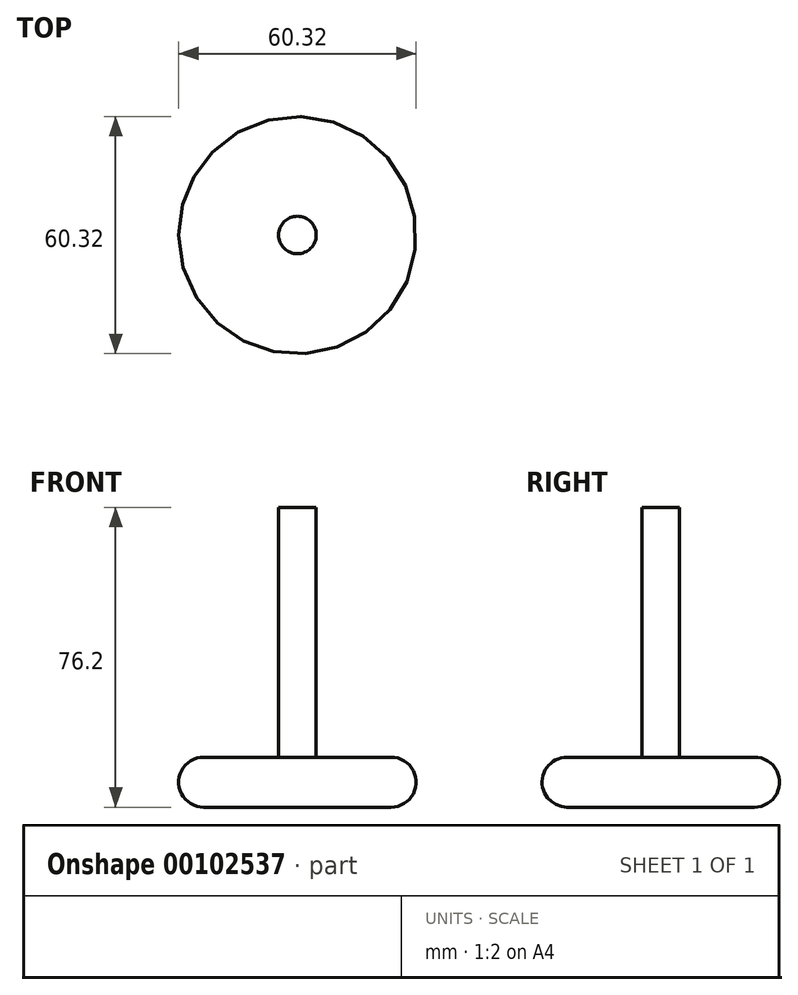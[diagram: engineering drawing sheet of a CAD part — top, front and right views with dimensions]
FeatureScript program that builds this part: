
annotation { "Feature Type Name" : "Feature", "Feature Type Description" : "" }
export const myFeature = defineFeature(function(context is Context, id is Id, definition is map)
    precondition{}
    {
        {
            var Q0;
            Q0=qCreatedBy(makeId("Front.planeOp"),FACE);
            var sketch = newSketch(context, id + "F0", { "sketchPlane" : qUnion([Q0])});
            skLineSegment(sketch, "E0", {"start": v(0, 0) * mm, "end": v(0, 76.2) * mm});
            skLineSegment(sketch, "E1", {"start": v(0, 76.2) * mm, "end": v(4.76, 76.2) * mm});
            skLineSegment(sketch, "E2", {"start": v(4.76, 76.2) * mm, "end": v(4.76, 12.7) * mm});
            skLineSegment(sketch, "E3", {"start": v(4.76, 12.7) * mm, "end": v(23.81, 12.7) * mm});
            skLineSegment(sketch, "E4", {"start": v(30.16, 6.35) * mm, "end": v(30.16, 6.35) * mm});
            skLineSegment(sketch, "E5", {"start": v(23.81, 0) * mm, "end": v(0, 0) * mm});
            skPoint(sketch, "E6.visualSharp", {"position": v(30.16, 12.7) * mm});
            skArc(sketch, "E6.filletArc", {"start": v(30.16, 6.35) * mm, "mid": v(28.3, 10.84) * mm, "end": v(23.81, 12.7) * mm});
            skPoint(sketch, "E7.visualSharp", {"position": v(30.16, 0) * mm});
            skArc(sketch, "E7.filletArc", {"start": v(23.81, 0) * mm, "mid": v(28.3, 1.86) * mm, "end": v(30.16, 6.35) * mm});
            skSolve(sketch);
        }
        {
            var Q0;
            Q0 = qSketchRegion(id + "F0", true);
            var Q1;
            Q1=sQuery(id+"F0.wireOp",EDGE,"E0");
            revolve(context, id + "F1", {"entities" : qUnion([Q0]), "axis" : qUnion([Q1]), "revolveType" : RevolveType.FULL});
        }
    });
